# Revit family: Deca_Tubo de ligação para bacia_1968.C.
name_source: partatom
category: Plumbing Fixtures
revit_build: Autodesk Revit 2013 (Build: 20120221_2030(x64)
units: mm (PartAtom-declared; Revit-internal decimal feet)

## types (6) — shared parameters
Aprovado por = Contino/quattroD
Atendimento ao Cliente = 0800-0117073
Consumo = Varia com a pressão
Criado por = Contino/quattroD
Código = 1968.C
Description = Tubo de ligação com anel expansor pra bacia
Diâmetro Água Fria = 15 mm  [stored 0.0492126 ft]
Flow Pressure = 0.00 psi
Linha = Tubo de ligação para bacia
Louça/Metais = Metal
Manufacturer = Deca
Material = Latão Cromado e Plástico de Engenharia
Model = 1968.C
Norma = ABNT NBR 10283:2003
Peso Liquido (Kg) = 0.236
Pressão = 2 A 40 mca
Produto = Tubo de ligação para bacia
Raio Água Fria = 8 mm  [stored 0.0262467 ft]
Segmento = Competitivo
URL = www.deca.com.br/produtos
Variações de COR = Cromado (1968.C); Branco (1968.E.BR); Bege (1968.E.BE); Preto Fosco (1968.F.PTO); Dourado (1968.D); Gold (1968.D.GLD)
Vendido Separadamente = Não Aplicável
zero-valued in all types: CWFU, Default Elevation

## per-type parameters (varying)
| type | Informações Complementares | Sifão |
| Cromado (1968.C) | Recomendável com pressão mínima de 10 m.c.a para aquecedor de passagem e de 2 m.c.a. para aquecedor de acumulação. | Deca CR10 Cromado Metal |
| Branco (1968.E.BR) | Recomendável com pressão mínima de 10 m.c.a para aquecedor de passagem e de 2 m.c.a. para aquecedor de acumulação. | Deca GE17 Branco Gelo Plástico |
| Bege (1968.E.BE) | Recomendável com pressão mínima de 10 m.c.a para aquecedor de passagem e de 2 m.c.a. para aquecedor de acumulação. | Deca Bege |
| Preto Fosco (1968.F.PTO) |  | Deca PR15 Preto Fosco Metal |
| Dourado (1968.D) | Recomendável com pressão mínima de 10 m.c.a para aquecedor de passagem e de 2 m.c.a. para aquecedor de acumulação. | Deca GL MT Gold Matte Metal |
| Gold (1968.D.GLD) | Recomendável com pressão mínima de 10 m.c.a para aquecedor de passagem e de 2 m.c.a. para aquecedor de acumulação. | Deca GLD Gold Metal |

note: [stored X ft] marks values corroborated as IEEE doubles in the binary element streams (Revit-internal decimal feet)

## geometry (parser evidence)
native form markers: Blend x10, Sweep x2
no freeform markers — native parametric forms only
